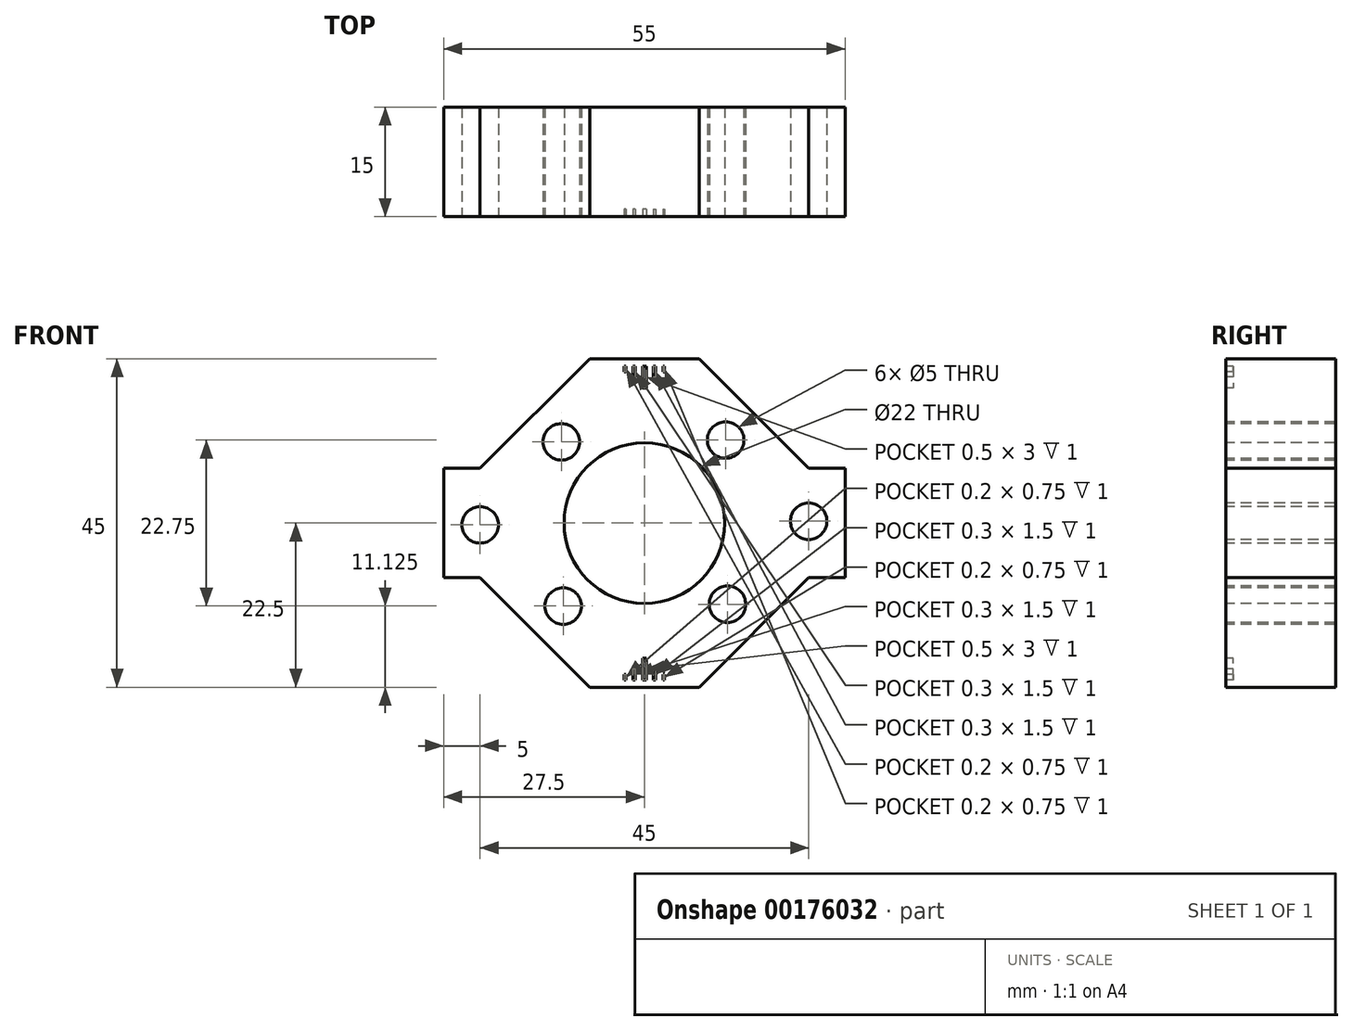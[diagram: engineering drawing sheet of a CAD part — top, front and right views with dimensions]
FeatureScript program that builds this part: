
annotation { "Feature Type Name" : "Feature", "Feature Type Description" : "" }
export const myFeature = defineFeature(function(context is Context, id is Id, definition is map)
    precondition{}
    {
        {
            var Q0;
            Q0=qCreatedBy(makeId("Front.planeOp"),FACE);
            var sketch = newSketch(context, id + "F0", { "sketchPlane" : qUnion([Q0])});
            skLineSegment(sketch, "E0.bottom", {"start": v(22.5, 22.5) * mm, "end": v(-22.5, 22.5) * mm});
            skLineSegment(sketch, "E0.top", {"start": v(22.5, -22.5) * mm, "end": v(-22.5, -22.5) * mm});
            skLineSegment(sketch, "E0.left", {"start": v(22.5, 22.5) * mm, "end": v(22.5, -22.5) * mm});
            skLineSegment(sketch, "E0.right", {"start": v(-22.5, 22.5) * mm, "end": v(-22.5, -22.5) * mm});
            skPoint(sketch, "E0.middle", {"position": v(0, 0) * mm});
            skSolve(sketch);
        }
        {
            var Q0;
            Q0 = qSketchRegion(id + "F0", true);
            extrude(context, id + "F1", {"entities" : qUnion([Q0]), "depth" : 15 * mm});
        }
        {
            var Q0;
            Q0=makeQuery(id+"F1.opExtrude","CAP_FACE",FACE,{"disambiguationData":[OSD([sQuery(id+"F0.wireOp",EDGE,"E0.bottom"),sQuery(id+"F0.wireOp",EDGE,"E0.top"),sQuery(id+"F0.wireOp",EDGE,"E0.left"),sQuery(id+"F0.wireOp",EDGE,"E0.right")])],"isStart":false});
            var sketch = newSketch(context, id + "F2", { "sketchPlane" : qUnion([Q0])});
            skCircle(sketch, "E1", {"center": v(0, 0) * mm, "radius": 11 * mm});
            skSolve(sketch);
        }
        {
            var Q0;
            Q0 = qSketchRegion(id + "F2", true);
            extrude(context, id + "F3", {"entities" : qUnion([Q0]), "operationType" : NewBodyOperationType.REMOVE, "endBound" : BoundingType.THROUGH_ALL, "oppositeDirection" : true, "depth" : 25 * mm});
        }
        {
            var Q0;
            Q0=makeQuery(id+"F1.opExtrude","CAP_FACE",FACE,{"disambiguationData":[OSD([sQuery(id+"F0.wireOp",EDGE,"E0.bottom"),sQuery(id+"F0.wireOp",EDGE,"E0.top"),sQuery(id+"F0.wireOp",EDGE,"E0.left"),sQuery(id+"F0.wireOp",EDGE,"E0.right")])],"isStart":false});
            var sketch = newSketch(context, id + "F4", { "sketchPlane" : qUnion([Q0])});
            skLineSegment(sketch, "E2", {"start": v(-22.5, 7.5) * mm, "end": v(-7.5, 22.5) * mm});
            skLineSegment(sketch, "E3", {"start": v(-7.5, 22.5) * mm, "end": v(-22.5, 22.5) * mm});
            skLineSegment(sketch, "E4", {"start": v(-22.5, 22.5) * mm, "end": v(-22.5, 7.5) * mm});
            skLineSegment(sketch, "E5", {"start": v(7.5, 22.5) * mm, "end": v(22.5, 7.5) * mm});
            skLineSegment(sketch, "E6", {"start": v(22.5, 7.5) * mm, "end": v(22.5, 22.5) * mm});
            skLineSegment(sketch, "E7", {"start": v(22.5, 22.5) * mm, "end": v(7.5, 22.5) * mm});
            skLineSegment(sketch, "E8", {"start": v(-7.5, -22.5) * mm, "end": v(-22.5, -7.5) * mm});
            skLineSegment(sketch, "E9", {"start": v(-22.5, -7.5) * mm, "end": v(-22.5, -22.5) * mm});
            skLineSegment(sketch, "E10", {"start": v(-22.5, -22.5) * mm, "end": v(-7.5, -22.5) * mm});
            skLineSegment(sketch, "E11", {"start": v(22.5, -7.5) * mm, "end": v(7.5, -22.5) * mm});
            skLineSegment(sketch, "E12", {"start": v(7.5, -22.5) * mm, "end": v(22.5, -22.5) * mm});
            skLineSegment(sketch, "E13", {"start": v(22.5, -22.5) * mm, "end": v(22.5, -7.5) * mm});
            skSolve(sketch);
        }
        {
            var Q0;
            Q0 = qSketchRegion(id + "F4", true);
            extrude(context, id + "F5", {"entities" : qUnion([Q0]), "operationType" : NewBodyOperationType.REMOVE, "endBound" : BoundingType.THROUGH_ALL, "oppositeDirection" : true, "depth" : 25 * mm});
        }
        {
            var Q0;
            Q0=makeQuery(id+"F1.opExtrude","CAP_FACE",FACE,{"disambiguationData":[OSD([sQuery(id+"F0.wireOp",EDGE,"E0.bottom"),sQuery(id+"F0.wireOp",EDGE,"E0.top"),sQuery(id+"F0.wireOp",EDGE,"E0.left"),sQuery(id+"F0.wireOp",EDGE,"E0.right")])],"isStart":false});
            var sketch = newSketch(context, id + "F6", { "sketchPlane" : qUnion([Q0])});
            skLineSegment(sketch, "E14.bottom", {"start": v(0.25, 21.5) * mm, "end": v(-0.25, 21.5) * mm});
            skLineSegment(sketch, "E14.left", {"start": v(0.25, 21.5) * mm, "end": v(0.25, 20) * mm});
            skLineSegment(sketch, "E14.right", {"start": v(-0.25, 21.5) * mm, "end": v(-0.25, 20) * mm});
            skPoint(sketch, "E14.middle", {"position": v(0, 20.75) * mm});
            skLineSegment(sketch, "E15.bottom", {"start": v(-1.25, 21.5) * mm, "end": v(-1.55, 21.5) * mm});
            skLineSegment(sketch, "E15.top", {"start": v(-1.25, 20) * mm, "end": v(-1.55, 20) * mm});
            skLineSegment(sketch, "E15.left", {"start": v(-1.25, 21.5) * mm, "end": v(-1.25, 20) * mm});
            skLineSegment(sketch, "E15.right", {"start": v(-1.55, 21.5) * mm, "end": v(-1.55, 20) * mm});
            skPoint(sketch, "E15.middle", {"position": v(-1.4, 20.75) * mm});
            skLineSegment(sketch, "E16.bottom", {"start": v(1.25, 21.5) * mm, "end": v(1.55, 21.5) * mm});
            skLineSegment(sketch, "E16.top", {"start": v(1.25, 20) * mm, "end": v(1.55, 20) * mm});
            skLineSegment(sketch, "E16.left", {"start": v(1.25, 21.5) * mm, "end": v(1.25, 20) * mm});
            skLineSegment(sketch, "E16.right", {"start": v(1.55, 21.5) * mm, "end": v(1.55, 20) * mm});
            skPoint(sketch, "E16.middle", {"position": v(1.4, 20.75) * mm});
            skLineSegment(sketch, "E17.top", {"start": v(-0.25, 18.5) * mm, "end": v(0.25, 18.5) * mm});
            skLineSegment(sketch, "E17.left", {"start": v(-0.25, 20) * mm, "end": v(-0.25, 18.5) * mm});
            skLineSegment(sketch, "E17.right", {"start": v(0.25, 20) * mm, "end": v(0.25, 18.5) * mm});
            skLineSegment(sketch, "E18.bottom", {"start": v(-2.55, 20.75) * mm, "end": v(-2.75, 20.75) * mm});
            skLineSegment(sketch, "E18.top", {"start": v(-2.55, 21.5) * mm, "end": v(-2.75, 21.5) * mm});
            skLineSegment(sketch, "E18.left", {"start": v(-2.55, 20.75) * mm, "end": v(-2.55, 21.5) * mm});
            skLineSegment(sketch, "E18.right", {"start": v(-2.75, 20.75) * mm, "end": v(-2.75, 21.5) * mm});
            skPoint(sketch, "E19.firstSnap0", {"position": v(1.55, 20.75) * mm});
            skLineSegment(sketch, "E19.bottom", {"start": v(2.55, 20.75) * mm, "end": v(2.75, 20.75) * mm});
            skLineSegment(sketch, "E19.top", {"start": v(2.55, 21.5) * mm, "end": v(2.75, 21.5) * mm});
            skLineSegment(sketch, "E19.left", {"start": v(2.55, 20.75) * mm, "end": v(2.55, 21.5) * mm});
            skLineSegment(sketch, "E19.right", {"start": v(2.75, 20.75) * mm, "end": v(2.75, 21.5) * mm});
            skLineSegment(sketch, "E20.MirrorCS", {"start": v(0.25, -21.5) * mm, "end": v(-0.25, -21.5) * mm});
            skLineSegment(sketch, "E21.MirrorCS", {"start": v(-1.25, -21.5) * mm, "end": v(-1.55, -21.5) * mm});
            skLineSegment(sketch, "E22.MirrorCS", {"start": v(-1.25, -20) * mm, "end": v(-1.55, -20) * mm});
            skLineSegment(sketch, "E23.MirrorCS", {"start": v(2.55, -20.75) * mm, "end": v(2.75, -20.75) * mm});
            skLineSegment(sketch, "E24.MirrorCS", {"start": v(-0.25, -18.5) * mm, "end": v(0.25, -18.5) * mm});
            skLineSegment(sketch, "E25.MirrorCS", {"start": v(1.25, -21.5) * mm, "end": v(1.55, -21.5) * mm});
            skLineSegment(sketch, "E26.MirrorCS", {"start": v(1.25, -20) * mm, "end": v(1.55, -20) * mm});
            skLineSegment(sketch, "E27.MirrorCS", {"start": v(-2.55, -21.5) * mm, "end": v(-2.75, -21.5) * mm});
            skLineSegment(sketch, "E28.MirrorCS", {"start": v(2.55, -21.5) * mm, "end": v(2.75, -21.5) * mm});
            skLineSegment(sketch, "E29.MirrorCS", {"start": v(-2.55, -20.75) * mm, "end": v(-2.75, -20.75) * mm});
            skLineSegment(sketch, "E30.MirrorCS", {"start": v(0.25, -21.5) * mm, "end": v(0.25, -20) * mm});
            skLineSegment(sketch, "E31.MirrorCS", {"start": v(-1.55, -21.5) * mm, "end": v(-1.55, -20) * mm});
            skPoint(sketch, "E32.MirrorP", {"position": v(1.55, -20.75) * mm});
            skLineSegment(sketch, "E33.MirrorCS", {"start": v(2.75, -20.75) * mm, "end": v(2.75, -21.5) * mm});
            skLineSegment(sketch, "E34.MirrorCS", {"start": v(2.55, -20.75) * mm, "end": v(2.55, -21.5) * mm});
            skLineSegment(sketch, "E35.MirrorCS", {"start": v(-0.25, -20) * mm, "end": v(-0.25, -18.5) * mm});
            skPoint(sketch, "E36.MirrorP", {"position": v(1.4, -20.75) * mm});
            skLineSegment(sketch, "E37.MirrorCS", {"start": v(-0.25, -21.5) * mm, "end": v(-0.25, -20) * mm});
            skLineSegment(sketch, "E38.MirrorCS", {"start": v(-2.55, -20.75) * mm, "end": v(-2.55, -21.5) * mm});
            skPoint(sketch, "E39.MirrorP", {"position": v(-1.4, -20.75) * mm});
            skLineSegment(sketch, "E40.MirrorCS", {"start": v(-1.25, -21.5) * mm, "end": v(-1.25, -20) * mm});
            skLineSegment(sketch, "E41.MirrorCS", {"start": v(1.25, -21.5) * mm, "end": v(1.25, -20) * mm});
            skPoint(sketch, "E42.MirrorP", {"position": v(0, -20.75) * mm});
            skLineSegment(sketch, "E43.MirrorCS", {"start": v(1.55, -21.5) * mm, "end": v(1.55, -20) * mm});
            skLineSegment(sketch, "E44.MirrorCS", {"start": v(-2.75, -20.75) * mm, "end": v(-2.75, -21.5) * mm});
            skLineSegment(sketch, "E45.MirrorCS", {"start": v(0.25, -20) * mm, "end": v(0.25, -18.5) * mm});
            skSolve(sketch);
        }
        {
            var Q0;
            Q0 = qSketchRegion(id + "F6", true);
            extrude(context, id + "F7", {"entities" : qUnion([Q0]), "operationType" : NewBodyOperationType.REMOVE, "oppositeDirection" : true, "depth" : 1 * mm});
        }
        {
            var Q0;
            Q0=makeQuery(id+"F1.opExtrude","SWEPT_FACE",FACE,{"disambiguationData":[OSD([sQuery(id+"F0.wireOp",EDGE,"E0.left")])]});
            extrude(context, id + "F8", {"entities" : qUnion([Q0]), "operationType" : NewBodyOperationType.ADD, "depth" : 5 * mm});
        }
        {
            var Q0;
            Q0=makeQuery(id+"F1.opExtrude","SWEPT_FACE",FACE,{"disambiguationData":[OSD([sQuery(id+"F0.wireOp",EDGE,"E0.right")])]});
            extrude(context, id + "F9", {"entities" : qUnion([Q0]), "operationType" : NewBodyOperationType.ADD, "depth" : 5 * mm});
        }
        {
            var Q0;
            {var subQ0=sQuery(id+"F0.wireOp",EDGE,"E0.right");var subQ1=sQuery(id+"F0.wireOp",EDGE,"E0.left");Q0=makeQuery(id+"F9.boolean.opBoolean","MERGE",FACE,{"derivedFrom":[makeQuery(id+"F8.boolean.opBoolean","MERGE",FACE,{"derivedFrom":[makeQuery(id+"F1.opExtrude","CAP_FACE",FACE,{"disambiguationData":[OSD([sQuery(id+"F0.wireOp",EDGE,"E0.bottom"),sQuery(id+"F0.wireOp",EDGE,"E0.top"),subQ1,subQ0])],"isStart":false}),makeQuery(id+"F8.opExtrude","SWEPT_FACE",FACE,{"disambiguationData":[OSD([subQ1]),TDD([makeQuery(id+"F1.opExtrude","CAP_EDGE",EDGE,{"disambiguationData":[OSD([subQ1])],"isStart":false})])]})]}),makeQuery(id+"F9.opExtrude","SWEPT_FACE",FACE,{"disambiguationData":[OSD([subQ0]),TDD([makeQuery(id+"F1.opExtrude","CAP_EDGE",EDGE,{"disambiguationData":[OSD([subQ0])],"isStart":false})])]})]});}
            var sketch = newSketch(context, id + "F10", { "sketchPlane" : qUnion([Q0])});
            skArc(sketch, "E46.cCircle", {"start": v(-12.77, -9.5) * mm, "mid": v(-11.13, -11.37) * mm, "end": v(-9.2, -12.98) * mm, "construction": true});
            skLineSegment(sketch, "E46.0", {"start": v(9.34, 13.12) * mm, "end": v(12.91, 9.63) * mm});
            skLineSegment(sketch, "E46.1", {"start": v(22.5, 0.25) * mm, "end": v(20.75, -1.54) * mm});
            skLineSegment(sketch, "E46.2", {"start": v(-9.34, -13.12) * mm, "end": v(-12.91, -9.63) * mm});
            skLineSegment(sketch, "E46.3", {"start": v(-22.5, -0.25) * mm, "end": v(-20.75, 1.54) * mm});
            skPoint(sketch, "E46.0.midPoint", {"position": v(11.12, 11.37) * mm});
            skCircle(sketch, "E47", {"center": v(-22.5, -0.25) * mm, "radius": 2.5 * mm});
            skCircle(sketch, "E48", {"center": v(22.5, 0.25) * mm, "radius": 2.5 * mm});
            skCircle(sketch, "E49", {"center": v(-11.38, 11.12) * mm, "radius": 2.5 * mm});
            skCircle(sketch, "E50", {"center": v(11.12, 11.37) * mm, "radius": 2.5 * mm});
            skCircle(sketch, "E51", {"center": v(-11.13, -11.38) * mm, "radius": 2.5 * mm});
            skCircle(sketch, "E52", {"center": v(11.37, -11.12) * mm, "radius": 2.5 * mm});
            skPoint(sketch, "E52.perimeterSnap0", {"position": v(11.37, -11.12) * mm});
            skPoint(sketch, "E52.perimeterSnap1", {"position": v(15, -15) * mm});
            skLineSegment(sketch, "E53.trimOffspring", {"start": v(-13.12, 9.34) * mm, "end": v(-9.63, 12.91) * mm});
            skLineSegment(sketch, "E54.trimOffspring", {"start": v(-20.71, -2) * mm, "end": v(-22.5, -0.25) * mm});
            skArc(sketch, "E55.trimOffspring", {"start": v(9.5, -12.77) * mm, "mid": v(11.37, -11.12) * mm, "end": v(12.98, -9.2) * mm, "construction": true});
            skPoint(sketch, "E56.orphan", {"position": v(0.25, -22.5) * mm});
            skArc(sketch, "E57.trimOffspring", {"start": v(12.77, 9.5) * mm, "mid": v(11.12, 11.37) * mm, "end": v(9.2, 12.98) * mm, "construction": true});
            skLineSegment(sketch, "E58.trimOffspring", {"start": v(13.12, -9.34) * mm, "end": v(9.63, -12.91) * mm});
            skLineSegment(sketch, "E59.trimOffspring", {"start": v(20.71, 2) * mm, "end": v(22.5, 0.25) * mm});
            skArc(sketch, "E60.trimOffspring", {"start": v(-9.5, 12.77) * mm, "mid": v(-11.37, 11.12) * mm, "end": v(-12.98, 9.2) * mm, "construction": true});
            skPoint(sketch, "E61.orphan", {"position": v(-0.25, 22.5) * mm});
            skSolve(sketch);
        }
        {
            var Q0;
            Q0 = qSketchRegion(id + "F10", true);
            extrude(context, id + "F11", {"entities" : qUnion([Q0]), "operationType" : NewBodyOperationType.REMOVE, "endBound" : BoundingType.THROUGH_ALL, "oppositeDirection" : true, "depth" : 25 * mm});
        }
    });
